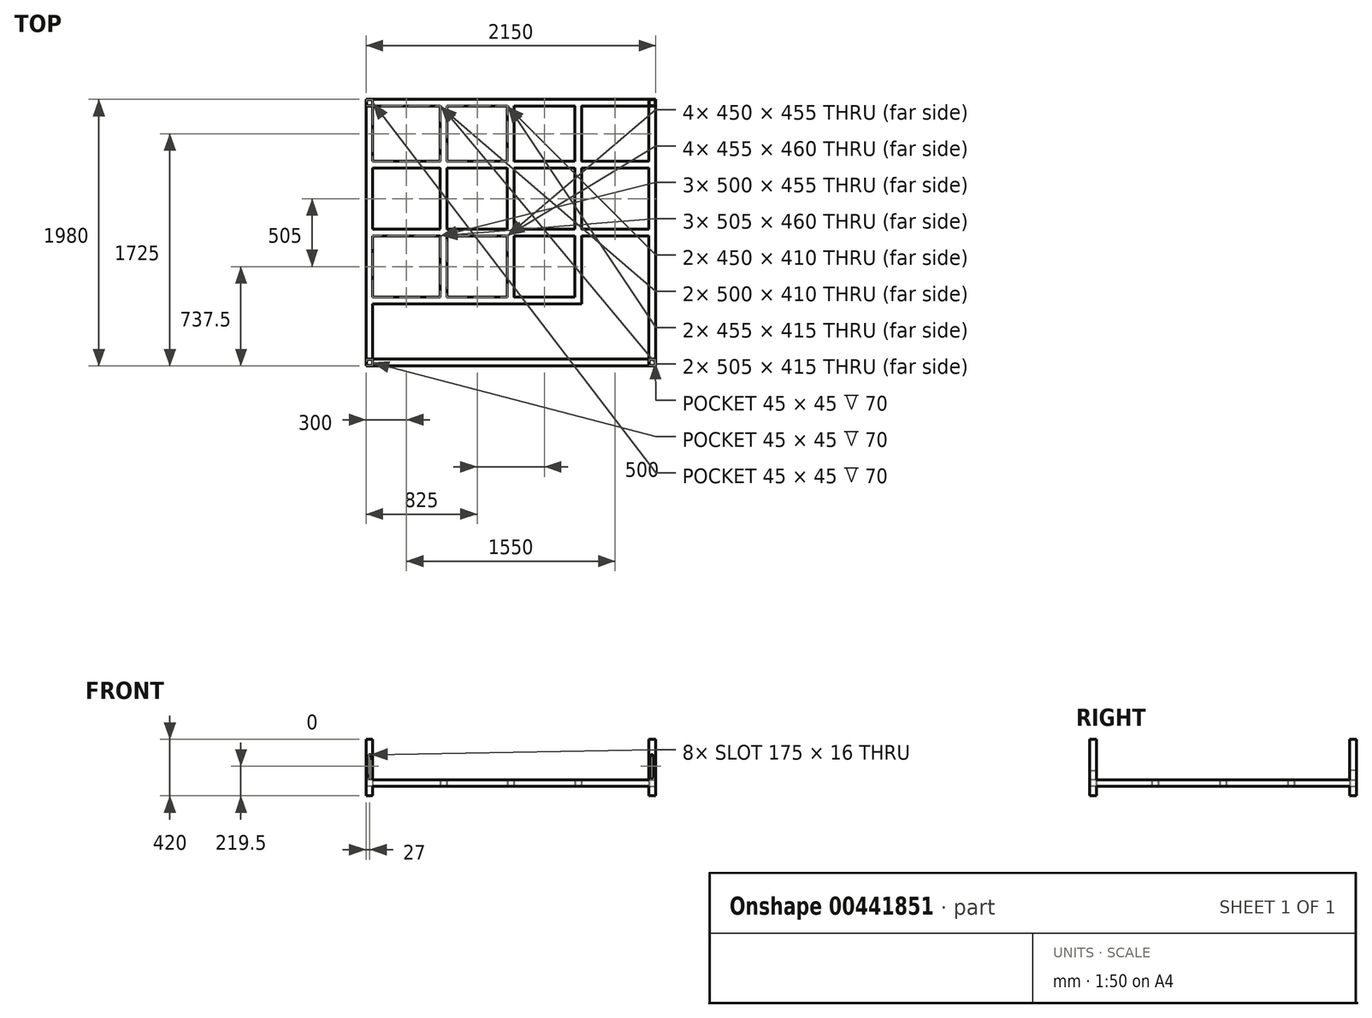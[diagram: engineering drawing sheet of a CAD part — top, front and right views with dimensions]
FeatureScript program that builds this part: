
annotation { "Feature Type Name" : "Feature", "Feature Type Description" : "" }
export const myFeature = defineFeature(function(context is Context, id is Id, definition is map)
    precondition{}
    {
        {
            var Q0;
            Q0=qCreatedBy(makeId("Top.planeOp"),FACE);
            var sketch = newSketch(context, id + "F0", { "sketchPlane" : qUnion([Q0])});
            skLineSegment(sketch, "E0.bottom", {"start": v(1075, 990) * mm, "end": v(-1075, 990) * mm});
            skLineSegment(sketch, "E0.top", {"start": v(1075, -990) * mm, "end": v(-1075, -990) * mm});
            skLineSegment(sketch, "E0.left", {"start": v(1075, 990) * mm, "end": v(1075, -990) * mm});
            skLineSegment(sketch, "E0.right", {"start": v(-1075, 990) * mm, "end": v(-1075, -990) * mm});
            skPoint(sketch, "E0.middle", {"position": v(0, 0) * mm});
            skLineSegment(sketch, "E1.bottom", {"start": v(1025, 940) * mm, "end": v(-1025, 940) * mm});
            skLineSegment(sketch, "E1.top", {"start": v(1025, -940) * mm, "end": v(-1025, -940) * mm});
            skLineSegment(sketch, "E1.left", {"start": v(1025, 940) * mm, "end": v(1025, -940) * mm});
            skLineSegment(sketch, "E1.right", {"start": v(-1025, 940) * mm, "end": v(-1025, -940) * mm});
            skLineSegment(sketch, "E2", {"start": v(-1025, 530) * mm, "end": v(1025, 530) * mm});
            skLineSegment(sketch, "E3", {"start": v(-1025, 480) * mm, "end": v(1025, 480) * mm});
            skLineSegment(sketch, "E4", {"start": v(-1025, 25) * mm, "end": v(1025, 25) * mm});
            skLineSegment(sketch, "E5", {"start": v(-1025, -25) * mm, "end": v(1025, -25) * mm});
            skLineSegment(sketch, "E6", {"start": v(-1025, -480) * mm, "end": v(1025, -480) * mm});
            skLineSegment(sketch, "E7", {"start": v(1025, -480) * mm, "end": v(1025, -530) * mm});
            skLineSegment(sketch, "E8", {"start": v(1025, -530) * mm, "end": v(-1025, -530) * mm});
            skLineSegment(sketch, "E9", {"start": v(-525, 940) * mm, "end": v(-525, -940) * mm});
            skLineSegment(sketch, "E10", {"start": v(-525, -940) * mm, "end": v(-475, -940) * mm});
            skLineSegment(sketch, "E11", {"start": v(-475, -940) * mm, "end": v(-475, 940) * mm});
            skLineSegment(sketch, "E12", {"start": v(-475, 940) * mm, "end": v(-25, 940) * mm});
            skLineSegment(sketch, "E13", {"start": v(-25, 940) * mm, "end": v(-25, -940) * mm});
            skLineSegment(sketch, "E14", {"start": v(-25, -940) * mm, "end": v(25, -940) * mm});
            skLineSegment(sketch, "E15", {"start": v(25, -940) * mm, "end": v(25, 940) * mm});
            skLineSegment(sketch, "E16", {"start": v(25, 940) * mm, "end": v(475, 940) * mm});
            skLineSegment(sketch, "E17", {"start": v(475, 940) * mm, "end": v(475, -940) * mm});
            skLineSegment(sketch, "E18", {"start": v(475, -940) * mm, "end": v(525, -940) * mm});
            skLineSegment(sketch, "E19", {"start": v(525, -940) * mm, "end": v(525, 940) * mm});
            skSolve(sketch);
        }
        {
            var Q0;
            Q0=makeQuery(id+"F0.imprint","IMPRINT",FACE,{"disambiguationData":[TD([[makeQuery(id+"F0.imprint","IMPRINT",EDGE,{"derivedFrom":sQuery(id+"F0.wireOp",EDGE,"E0.bottom")}),1.0]])]});
            var Q1;
            {var subQ0=sQuery(id+"F0.wireOp",EDGE,"E9");var subQ1=sQuery(id+"F0.wireOp",EDGE,"E2");var subQ2=makeQuery(id+"F0.imprint","INTERSECT",VERTEX,{"derivedFrom":[subQ1,subQ0]});Q1=makeQuery(id+"F0.imprint","IMPRINT",FACE,{"disambiguationData":[TD([[makeQuery(id+"F0.imprint","IMPRINT",EDGE,{"disambiguationData":[TD([[subQ2,-1.0]])],"derivedFrom":subQ1}),-1.0]])]});}
            var Q2;
            {var subQ0=sQuery(id+"F0.wireOp",EDGE,"E9");var subQ1=sQuery(id+"F0.wireOp",EDGE,"E4");var subQ2=makeQuery(id+"F0.imprint","INTERSECT",VERTEX,{"derivedFrom":[subQ1,subQ0]});Q2=makeQuery(id+"F0.imprint","IMPRINT",FACE,{"disambiguationData":[TD([[makeQuery(id+"F0.imprint","IMPRINT",EDGE,{"disambiguationData":[TD([[subQ2,-1.0]])],"derivedFrom":subQ1}),-1.0]])]});}
            var Q3;
            {var subQ0=sQuery(id+"F0.wireOp",EDGE,"E11");var subQ1=sQuery(id+"F0.wireOp",EDGE,"E2");var subQ2=makeQuery(id+"F0.imprint","INTERSECT",VERTEX,{"derivedFrom":[subQ1,subQ0]});Q3=makeQuery(id+"F0.imprint","IMPRINT",FACE,{"disambiguationData":[TD([[makeQuery(id+"F0.imprint","IMPRINT",EDGE,{"disambiguationData":[TD([[subQ2,-1.0]])],"derivedFrom":subQ1}),-1.0]])]});}
            var Q4;
            {var subQ0=sQuery(id+"F0.wireOp",EDGE,"E13");var subQ1=sQuery(id+"F0.wireOp",EDGE,"E2");var subQ2=makeQuery(id+"F0.imprint","INTERSECT",VERTEX,{"derivedFrom":[subQ1,subQ0]});Q4=makeQuery(id+"F0.imprint","IMPRINT",FACE,{"disambiguationData":[TD([[makeQuery(id+"F0.imprint","IMPRINT",EDGE,{"disambiguationData":[TD([[subQ2,-1.0]])],"derivedFrom":subQ1}),-1.0]])]});}
            var Q5;
            {var subQ0=sQuery(id+"F0.wireOp",EDGE,"E15");var subQ1=sQuery(id+"F0.wireOp",EDGE,"E2");var subQ2=makeQuery(id+"F0.imprint","INTERSECT",VERTEX,{"derivedFrom":[subQ1,subQ0]});Q5=makeQuery(id+"F0.imprint","IMPRINT",FACE,{"disambiguationData":[TD([[makeQuery(id+"F0.imprint","IMPRINT",EDGE,{"disambiguationData":[TD([[subQ2,-1.0]])],"derivedFrom":subQ1}),-1.0]])]});}
            var Q6;
            {var subQ0=sQuery(id+"F0.wireOp",EDGE,"E17");var subQ1=sQuery(id+"F0.wireOp",EDGE,"E2");var subQ2=makeQuery(id+"F0.imprint","INTERSECT",VERTEX,{"derivedFrom":[subQ1,subQ0]});Q6=makeQuery(id+"F0.imprint","IMPRINT",FACE,{"disambiguationData":[TD([[makeQuery(id+"F0.imprint","IMPRINT",EDGE,{"disambiguationData":[TD([[subQ2,-1.0]])],"derivedFrom":subQ1}),-1.0]])]});}
            var Q7;
            {var subQ0=sQuery(id+"F0.wireOp",EDGE,"E2");var subQ1=sQuery(id+"F0.wireOp",EDGE,"E1.left");var subQ2=makeQuery(id+"F0.imprint","INTERSECT",VERTEX,{"derivedFrom":[subQ1,subQ0]});Q7=makeQuery(id+"F0.imprint","IMPRINT",FACE,{"disambiguationData":[TD([[makeQuery(id+"F0.imprint","IMPRINT",EDGE,{"disambiguationData":[TD([[subQ2,-1.0]])],"derivedFrom":subQ1}),-1.0]])]});}
            var Q8;
            {var subQ0=sQuery(id+"F0.wireOp",EDGE,"E17");var subQ5=sQuery(id+"F0.wireOp",EDGE,"E2");var subQ7=makeQuery(id+"F0.imprint","INTERSECT",VERTEX,{"derivedFrom":[subQ5,subQ0]});Q8=makeQuery(id+"F0.imprint","IMPRINT",FACE,{"disambiguationData":[TD([[makeQuery(id+"F0.imprint","IMPRINT",EDGE,{"disambiguationData":[TD([[subQ7,-1.0]])],"derivedFrom":subQ5}),1.0]])]});}
            var Q9;
            {var subQ0=sQuery(id+"F0.wireOp",EDGE,"E13");var subQ5=sQuery(id+"F0.wireOp",EDGE,"E2");var subQ6=makeQuery(id+"F0.imprint","INTERSECT",VERTEX,{"derivedFrom":[subQ5,subQ0]});Q9=makeQuery(id+"F0.imprint","IMPRINT",FACE,{"disambiguationData":[TD([[makeQuery(id+"F0.imprint","IMPRINT",EDGE,{"disambiguationData":[TD([[subQ6,-1.0]])],"derivedFrom":subQ5}),1.0]])]});}
            var Q10;
            {var subQ0=sQuery(id+"F0.wireOp",EDGE,"E9");var subQ5=sQuery(id+"F0.wireOp",EDGE,"E2");var subQ6=makeQuery(id+"F0.imprint","INTERSECT",VERTEX,{"derivedFrom":[subQ5,subQ0]});Q10=makeQuery(id+"F0.imprint","IMPRINT",FACE,{"disambiguationData":[TD([[makeQuery(id+"F0.imprint","IMPRINT",EDGE,{"disambiguationData":[TD([[subQ6,-1.0]])],"derivedFrom":subQ5}),1.0]])]});}
            var Q11;
            {var subQ0=sQuery(id+"F0.wireOp",EDGE,"E2");var subQ1=sQuery(id+"F0.wireOp",EDGE,"E1.right");var subQ2=makeQuery(id+"F0.imprint","INTERSECT",VERTEX,{"derivedFrom":[subQ1,subQ0]});Q11=makeQuery(id+"F0.imprint","IMPRINT",FACE,{"disambiguationData":[TD([[makeQuery(id+"F0.imprint","IMPRINT",EDGE,{"disambiguationData":[TD([[subQ2,-1.0]])],"derivedFrom":subQ1}),1.0]])]});}
            var Q12;
            {var subQ0=sQuery(id+"F0.wireOp",EDGE,"E4");var subQ1=sQuery(id+"F0.wireOp",EDGE,"E1.right");var subQ2=makeQuery(id+"F0.imprint","INTERSECT",VERTEX,{"derivedFrom":[subQ1,subQ0]});Q12=makeQuery(id+"F0.imprint","IMPRINT",FACE,{"disambiguationData":[TD([[makeQuery(id+"F0.imprint","IMPRINT",EDGE,{"disambiguationData":[TD([[subQ2,-1.0]])],"derivedFrom":subQ1}),1.0]])]});}
            var Q13;
            {var subQ0=sQuery(id+"F0.wireOp",EDGE,"E9");var subQ1=sQuery(id+"F0.wireOp",EDGE,"E3");var subQ2=makeQuery(id+"F0.imprint","INTERSECT",VERTEX,{"derivedFrom":[subQ1,subQ0]});Q13=makeQuery(id+"F0.imprint","IMPRINT",FACE,{"disambiguationData":[TD([[makeQuery(id+"F0.imprint","IMPRINT",EDGE,{"disambiguationData":[TD([[subQ2,-1.0]])],"derivedFrom":subQ1}),-1.0]])]});}
            var Q14;
            {var subQ0=sQuery(id+"F0.wireOp",EDGE,"E9");var subQ1=sQuery(id+"F0.wireOp",EDGE,"E5");var subQ2=makeQuery(id+"F0.imprint","INTERSECT",VERTEX,{"derivedFrom":[subQ1,subQ0]});Q14=makeQuery(id+"F0.imprint","IMPRINT",FACE,{"disambiguationData":[TD([[makeQuery(id+"F0.imprint","IMPRINT",EDGE,{"disambiguationData":[TD([[subQ2,-1.0]])],"derivedFrom":subQ1}),-1.0]])]});}
            var Q15;
            {var subQ0=sQuery(id+"F0.wireOp",EDGE,"E11");var subQ1=sQuery(id+"F0.wireOp",EDGE,"E4");var subQ2=makeQuery(id+"F0.imprint","INTERSECT",VERTEX,{"derivedFrom":[subQ1,subQ0]});Q15=makeQuery(id+"F0.imprint","IMPRINT",FACE,{"disambiguationData":[TD([[makeQuery(id+"F0.imprint","IMPRINT",EDGE,{"disambiguationData":[TD([[subQ2,-1.0]])],"derivedFrom":subQ1}),-1.0]])]});}
            var Q16;
            {var subQ0=sQuery(id+"F0.wireOp",EDGE,"E13");var subQ1=sQuery(id+"F0.wireOp",EDGE,"E3");var subQ2=makeQuery(id+"F0.imprint","INTERSECT",VERTEX,{"derivedFrom":[subQ1,subQ0]});Q16=makeQuery(id+"F0.imprint","IMPRINT",FACE,{"disambiguationData":[TD([[makeQuery(id+"F0.imprint","IMPRINT",EDGE,{"disambiguationData":[TD([[subQ2,-1.0]])],"derivedFrom":subQ1}),-1.0]])]});}
            var Q17;
            {var subQ0=sQuery(id+"F0.wireOp",EDGE,"E15");var subQ1=sQuery(id+"F0.wireOp",EDGE,"E4");var subQ2=makeQuery(id+"F0.imprint","INTERSECT",VERTEX,{"derivedFrom":[subQ1,subQ0]});Q17=makeQuery(id+"F0.imprint","IMPRINT",FACE,{"disambiguationData":[TD([[makeQuery(id+"F0.imprint","IMPRINT",EDGE,{"disambiguationData":[TD([[subQ2,-1.0]])],"derivedFrom":subQ1}),-1.0]])]});}
            var Q18;
            {var subQ0=sQuery(id+"F0.wireOp",EDGE,"E17");var subQ1=sQuery(id+"F0.wireOp",EDGE,"E4");var subQ2=makeQuery(id+"F0.imprint","INTERSECT",VERTEX,{"derivedFrom":[subQ1,subQ0]});Q18=makeQuery(id+"F0.imprint","IMPRINT",FACE,{"disambiguationData":[TD([[makeQuery(id+"F0.imprint","IMPRINT",EDGE,{"disambiguationData":[TD([[subQ2,-1.0]])],"derivedFrom":subQ1}),-1.0]])]});}
            var Q19;
            {var subQ0=sQuery(id+"F0.wireOp",EDGE,"E17");var subQ1=sQuery(id+"F0.wireOp",EDGE,"E3");var subQ2=makeQuery(id+"F0.imprint","INTERSECT",VERTEX,{"derivedFrom":[subQ1,subQ0]});Q19=makeQuery(id+"F0.imprint","IMPRINT",FACE,{"disambiguationData":[TD([[makeQuery(id+"F0.imprint","IMPRINT",EDGE,{"disambiguationData":[TD([[subQ2,-1.0]])],"derivedFrom":subQ1}),-1.0]])]});}
            var Q20;
            {var subQ0=sQuery(id+"F0.wireOp",EDGE,"E4");var subQ1=sQuery(id+"F0.wireOp",EDGE,"E1.left");var subQ2=makeQuery(id+"F0.imprint","INTERSECT",VERTEX,{"derivedFrom":[subQ1,subQ0]});Q20=makeQuery(id+"F0.imprint","IMPRINT",FACE,{"disambiguationData":[TD([[makeQuery(id+"F0.imprint","IMPRINT",EDGE,{"disambiguationData":[TD([[subQ2,-1.0]])],"derivedFrom":subQ1}),-1.0]])]});}
            var Q21;
            {var subQ0=sQuery(id+"F0.wireOp",EDGE,"E17");var subQ1=sQuery(id+"F0.wireOp",EDGE,"E5");var subQ2=makeQuery(id+"F0.imprint","INTERSECT",VERTEX,{"derivedFrom":[subQ1,subQ0]});Q21=makeQuery(id+"F0.imprint","IMPRINT",FACE,{"disambiguationData":[TD([[makeQuery(id+"F0.imprint","IMPRINT",EDGE,{"disambiguationData":[TD([[subQ2,-1.0]])],"derivedFrom":subQ1}),-1.0]])]});}
            var Q22;
            {var subQ0=sQuery(id+"F0.wireOp",EDGE,"E7");Q22=makeQuery(id+"F0.imprint","IMPRINT",FACE,{"disambiguationData":[TD([[makeQuery(id+"F0.imprint","IMPRINT",EDGE,{"derivedFrom":subQ0}),-1.0]])]});}
            var Q23;
            {var subQ0=sQuery(id+"F0.wireOp",EDGE,"E17");var subQ1=sQuery(id+"F0.wireOp",EDGE,"E6");var subQ2=makeQuery(id+"F0.imprint","INTERSECT",VERTEX,{"derivedFrom":[subQ1,subQ0]});Q23=makeQuery(id+"F0.imprint","IMPRINT",FACE,{"disambiguationData":[TD([[makeQuery(id+"F0.imprint","IMPRINT",EDGE,{"disambiguationData":[TD([[subQ2,-1.0]])],"derivedFrom":subQ1}),-1.0]])]});}
            var Q24;
            {var subQ5=sQuery(id+"F0.wireOp",EDGE,"E18");Q24=makeQuery(id+"F0.imprint","IMPRINT",FACE,{"disambiguationData":[TD([[makeQuery(id+"F0.imprint","IMPRINT",EDGE,{"derivedFrom":subQ5}),1.0]])]});}
            var Q25;
            {var subQ0=sQuery(id+"F0.wireOp",EDGE,"E15");var subQ1=sQuery(id+"F0.wireOp",EDGE,"E6");var subQ2=makeQuery(id+"F0.imprint","INTERSECT",VERTEX,{"derivedFrom":[subQ1,subQ0]});Q25=makeQuery(id+"F0.imprint","IMPRINT",FACE,{"disambiguationData":[TD([[makeQuery(id+"F0.imprint","IMPRINT",EDGE,{"disambiguationData":[TD([[subQ2,-1.0]])],"derivedFrom":subQ1}),-1.0]])]});}
            var Q26;
            {var subQ0=sQuery(id+"F0.wireOp",EDGE,"E13");var subQ1=sQuery(id+"F0.wireOp",EDGE,"E6");var subQ2=makeQuery(id+"F0.imprint","INTERSECT",VERTEX,{"derivedFrom":[subQ1,subQ0]});Q26=makeQuery(id+"F0.imprint","IMPRINT",FACE,{"disambiguationData":[TD([[makeQuery(id+"F0.imprint","IMPRINT",EDGE,{"disambiguationData":[TD([[subQ2,-1.0]])],"derivedFrom":subQ1}),-1.0]])]});}
            var Q27;
            {var subQ0=sQuery(id+"F0.wireOp",EDGE,"E13");var subQ1=sQuery(id+"F0.wireOp",EDGE,"E5");var subQ2=makeQuery(id+"F0.imprint","INTERSECT",VERTEX,{"derivedFrom":[subQ1,subQ0]});Q27=makeQuery(id+"F0.imprint","IMPRINT",FACE,{"disambiguationData":[TD([[makeQuery(id+"F0.imprint","IMPRINT",EDGE,{"disambiguationData":[TD([[subQ2,-1.0]])],"derivedFrom":subQ1}),-1.0]])]});}
            var Q28;
            {var subQ5=sQuery(id+"F0.wireOp",EDGE,"E14");Q28=makeQuery(id+"F0.imprint","IMPRINT",FACE,{"disambiguationData":[TD([[makeQuery(id+"F0.imprint","IMPRINT",EDGE,{"derivedFrom":subQ5}),1.0]])]});}
            var Q29;
            {var subQ0=sQuery(id+"F0.wireOp",EDGE,"E11");var subQ1=sQuery(id+"F0.wireOp",EDGE,"E6");var subQ2=makeQuery(id+"F0.imprint","INTERSECT",VERTEX,{"derivedFrom":[subQ1,subQ0]});Q29=makeQuery(id+"F0.imprint","IMPRINT",FACE,{"disambiguationData":[TD([[makeQuery(id+"F0.imprint","IMPRINT",EDGE,{"disambiguationData":[TD([[subQ2,-1.0]])],"derivedFrom":subQ1}),-1.0]])]});}
            var Q30;
            {var subQ0=sQuery(id+"F0.wireOp",EDGE,"E9");var subQ1=sQuery(id+"F0.wireOp",EDGE,"E6");var subQ2=makeQuery(id+"F0.imprint","INTERSECT",VERTEX,{"derivedFrom":[subQ1,subQ0]});Q30=makeQuery(id+"F0.imprint","IMPRINT",FACE,{"disambiguationData":[TD([[makeQuery(id+"F0.imprint","IMPRINT",EDGE,{"disambiguationData":[TD([[subQ2,-1.0]])],"derivedFrom":subQ1}),-1.0]])]});}
            var Q31;
            {var subQ0=sQuery(id+"F0.wireOp",EDGE,"E6");var subQ1=sQuery(id+"F0.wireOp",EDGE,"E1.right");var subQ2=makeQuery(id+"F0.imprint","INTERSECT",VERTEX,{"derivedFrom":[subQ1,subQ0]});Q31=makeQuery(id+"F0.imprint","IMPRINT",FACE,{"disambiguationData":[TD([[makeQuery(id+"F0.imprint","IMPRINT",EDGE,{"disambiguationData":[TD([[subQ2,-1.0]])],"derivedFrom":subQ1}),1.0]])]});}
            var Q32;
            {var subQ5=sQuery(id+"F0.wireOp",EDGE,"E10");Q32=makeQuery(id+"F0.imprint","IMPRINT",FACE,{"disambiguationData":[TD([[makeQuery(id+"F0.imprint","IMPRINT",EDGE,{"derivedFrom":subQ5}),1.0]])]});}
            var Q33;
            {var subQ0=sQuery(id+"F0.wireOp",EDGE,"E13");var subQ1=sQuery(id+"F0.wireOp",EDGE,"E4");var subQ2=makeQuery(id+"F0.imprint","INTERSECT",VERTEX,{"derivedFrom":[subQ1,subQ0]});Q33=makeQuery(id+"F0.imprint","IMPRINT",FACE,{"disambiguationData":[TD([[makeQuery(id+"F0.imprint","IMPRINT",EDGE,{"disambiguationData":[TD([[subQ2,-1.0]])],"derivedFrom":subQ1}),-1.0]])]});}
            extrude(context, id + "F1", {"entities" : qUnion([Q0, Q1, Q2, Q3, Q4, Q5, Q6, Q7, Q8, Q9, Q10, Q11, Q12, Q13, Q14, Q15, Q16, Q17, Q18, Q19, Q20, Q21, Q22, Q23, Q24, Q25, Q26, Q27, Q28, Q29, Q30, Q31, Q32, Q33]), "depth" : 50 * mm});
        }
        {
            var Q0;
            Q0=makeQuery(id+"F1.opExtrude","CAP_FACE",FACE,{"disambiguationData":[OSD([sQuery(id+"F0.wireOp",EDGE,"E0.bottom"),sQuery(id+"F0.wireOp",EDGE,"E0.top"),sQuery(id+"F0.wireOp",EDGE,"E0.left"),sQuery(id+"F0.wireOp",EDGE,"E0.right"),sQuery(id+"F0.wireOp",EDGE,"E1.bottom"),sQuery(id+"F0.wireOp",EDGE,"E1.top"),sQuery(id+"F0.wireOp",EDGE,"E1.left"),sQuery(id+"F0.wireOp",EDGE,"E1.right"),sQuery(id+"F0.wireOp",EDGE,"E2"),sQuery(id+"F0.wireOp",EDGE,"E3"),sQuery(id+"F0.wireOp",EDGE,"E4"),sQuery(id+"F0.wireOp",EDGE,"E5"),sQuery(id+"F0.wireOp",EDGE,"E6"),sQuery(id+"F0.wireOp",EDGE,"E8"),sQuery(id+"F0.wireOp",EDGE,"E9"),sQuery(id+"F0.wireOp",EDGE,"E11"),sQuery(id+"F0.wireOp",EDGE,"E12"),sQuery(id+"F0.wireOp",EDGE,"E13"),sQuery(id+"F0.wireOp",EDGE,"E15"),sQuery(id+"F0.wireOp",EDGE,"E16"),sQuery(id+"F0.wireOp",EDGE,"E17"),sQuery(id+"F0.wireOp",EDGE,"E19")])],"isStart":false});
            var sketch = newSketch(context, id + "F2", { "sketchPlane" : qUnion([Q0])});
            skLineSegment(sketch, "E20.bottom", {"start": v(1075, 990) * mm, "end": v(1025, 990) * mm});
            skLineSegment(sketch, "E20.top", {"start": v(1075, 940) * mm, "end": v(1025, 940) * mm});
            skLineSegment(sketch, "E20.left", {"start": v(1075, 990) * mm, "end": v(1075, 940) * mm});
            skLineSegment(sketch, "E20.right", {"start": v(1025, 990) * mm, "end": v(1025, 940) * mm});
            skLineSegment(sketch, "E21.bottom", {"start": v(1075, -990) * mm, "end": v(1025, -990) * mm});
            skLineSegment(sketch, "E21.top", {"start": v(1075, -940) * mm, "end": v(1025, -940) * mm});
            skLineSegment(sketch, "E21.left", {"start": v(1075, -990) * mm, "end": v(1075, -940) * mm});
            skLineSegment(sketch, "E21.right", {"start": v(1025, -990) * mm, "end": v(1025, -940) * mm});
            skLineSegment(sketch, "E22.bottom", {"start": v(-1075, -990) * mm, "end": v(-1025, -990) * mm});
            skLineSegment(sketch, "E22.top", {"start": v(-1075, -940) * mm, "end": v(-1025, -940) * mm});
            skLineSegment(sketch, "E22.left", {"start": v(-1075, -990) * mm, "end": v(-1075, -940) * mm});
            skLineSegment(sketch, "E22.right", {"start": v(-1025, -990) * mm, "end": v(-1025, -940) * mm});
            skLineSegment(sketch, "E23.bottom", {"start": v(-1075, 990) * mm, "end": v(-1025, 990) * mm});
            skLineSegment(sketch, "E23.top", {"start": v(-1075, 940) * mm, "end": v(-1025, 940) * mm});
            skLineSegment(sketch, "E23.left", {"start": v(-1075, 990) * mm, "end": v(-1075, 940) * mm});
            skLineSegment(sketch, "E23.right", {"start": v(-1025, 990) * mm, "end": v(-1025, 940) * mm});
            skSolve(sketch);
        }
        {
            var Q0;
            Q0 = qSketchRegion(id + "F2", true);
            extrude(context, id + "F3", {"entities" : qUnion([Q0]), "operationType" : NewBodyOperationType.ADD, "depth" : 300 * mm, "hasSecondDirection" : true, "secondDirectionOppositeDirection" : true, "secondDirectionDepth" : 120 * mm});
        }
        {
            var Q0;
            Q0=makeQuery(id+"F3.opExtrude","CAP_FACE",FACE,{"disambiguationData":[OSD([sQuery(id+"F2.wireOp",EDGE,"E22.bottom"),sQuery(id+"F2.wireOp",EDGE,"E22.top"),sQuery(id+"F2.wireOp",EDGE,"E22.left"),sQuery(id+"F2.wireOp",EDGE,"E22.right")])],"isStart":false});
            var Q1;
            Q1=makeQuery(id+"F3.opExtrude","CAP_FACE",FACE,{"disambiguationData":[OSD([sQuery(id+"F2.wireOp",EDGE,"E21.bottom"),sQuery(id+"F2.wireOp",EDGE,"E21.top"),sQuery(id+"F2.wireOp",EDGE,"E21.left"),sQuery(id+"F2.wireOp",EDGE,"E21.right")])],"isStart":false});
            var Q2;
            Q2=makeQuery(id+"F3.opExtrude","CAP_FACE",FACE,{"disambiguationData":[OSD([sQuery(id+"F2.wireOp",EDGE,"E20.bottom"),sQuery(id+"F2.wireOp",EDGE,"E20.top"),sQuery(id+"F2.wireOp",EDGE,"E20.left"),sQuery(id+"F2.wireOp",EDGE,"E20.right")])],"isStart":false});
            var Q3;
            Q3=makeQuery(id+"F3.opExtrude","CAP_FACE",FACE,{"disambiguationData":[OSD([sQuery(id+"F2.wireOp",EDGE,"E23.bottom"),sQuery(id+"F2.wireOp",EDGE,"E23.top"),sQuery(id+"F2.wireOp",EDGE,"E23.left"),sQuery(id+"F2.wireOp",EDGE,"E23.right")])],"isStart":false});
            shell(context, id + "F4", {"entities" : qUnion([Q0, Q1, Q2, Q3]), "thickness" : 2.5 * mm});
        }
        {
            var Q0;
            {var subQ6=sQuery(id+"F2.wireOp",EDGE,"E22.bottom");var subQ7=sQuery(id+"F2.wireOp",EDGE,"E22.right");var subQ8=sQuery(id+"F2.wireOp",EDGE,"E22.top");Q0=makeQuery(id+"F3.boolean.opBoolean","SPLIT",FACE,{"disambiguationData":[TD([makeQuery(id+"F3.opExtrude","CAP_FACE",FACE,{"disambiguationData":[OSD([subQ6,subQ8,sQuery(id+"F2.wireOp",EDGE,"E22.left"),subQ7])],"isStart":false})])],"derivedFrom":makeQuery(id+"F3.opExtrude","SWEPT_FACE",FACE,{"disambiguationData":[OSD([subQ7])]})});}
            var sketch = newSketch(context, id + "F5", { "sketchPlane" : qUnion([Q0])});
            skLineSegment(sketch, "E24.bottom", {"start": v(-987.5, 350) * mm, "end": v(-942.5, 350) * mm});
            skLineSegment(sketch, "E24.top", {"start": v(-987.5, 120) * mm, "end": v(-942.5, 120) * mm});
            skLineSegment(sketch, "E24.left", {"start": v(-987.5, 350) * mm, "end": v(-987.5, 120) * mm});
            skLineSegment(sketch, "E24.right", {"start": v(-942.5, 350) * mm, "end": v(-942.5, 120) * mm});
            skSolve(sketch);
        }
        {
            var Q0;
            Q0=makeQuery(id+"F5.imprint","IMPRINT",FACE,{"disambiguationData":[TD([[makeQuery(id+"F5.imprint","IMPRINT",EDGE,{"derivedFrom":sQuery(id+"F5.wireOp",EDGE,"E24.bottom")}),-1.0]])]});
            extrude(context, id + "F6", {"entities" : qUnion([Q0]), "operationType" : NewBodyOperationType.REMOVE, "oppositeDirection" : true, "depth" : 25 * mm});
        }
        {
            var Q0;
            {var subQ6=sQuery(id+"F2.wireOp",EDGE,"E23.top");var subQ7=sQuery(id+"F2.wireOp",EDGE,"E23.bottom");var subQ8=sQuery(id+"F2.wireOp",EDGE,"E23.right");Q0=makeQuery(id+"F3.boolean.opBoolean","SPLIT",FACE,{"disambiguationData":[TD([makeQuery(id+"F3.opExtrude","CAP_FACE",FACE,{"disambiguationData":[OSD([subQ7,subQ6,sQuery(id+"F2.wireOp",EDGE,"E23.left"),subQ8])],"isStart":false})])],"derivedFrom":makeQuery(id+"F3.opExtrude","SWEPT_FACE",FACE,{"disambiguationData":[OSD([subQ8])]})});}
            var sketch = newSketch(context, id + "F7", { "sketchPlane" : qUnion([Q0])});
            skLineSegment(sketch, "E25.bottom", {"start": v(942.5, 350) * mm, "end": v(987.5, 350) * mm});
            skLineSegment(sketch, "E25.top", {"start": v(942.5, 120) * mm, "end": v(987.5, 120) * mm});
            skLineSegment(sketch, "E25.left", {"start": v(942.5, 350) * mm, "end": v(942.5, 120) * mm});
            skLineSegment(sketch, "E25.right", {"start": v(987.5, 350) * mm, "end": v(987.5, 120) * mm});
            skSolve(sketch);
        }
        {
            var Q0;
            Q0=makeQuery(id+"F7.imprint","IMPRINT",FACE,{"disambiguationData":[TD([[makeQuery(id+"F7.imprint","IMPRINT",EDGE,{"derivedFrom":sQuery(id+"F7.wireOp",EDGE,"E25.bottom")}),1.0]])]});
            extrude(context, id + "F8", {"entities" : qUnion([Q0]), "operationType" : NewBodyOperationType.REMOVE, "oppositeDirection" : true, "depth" : 25 * mm});
        }
        {
            var Q0;
            {var subQ6=sQuery(id+"F2.wireOp",EDGE,"E21.bottom");var subQ7=sQuery(id+"F2.wireOp",EDGE,"E21.right");var subQ8=sQuery(id+"F2.wireOp",EDGE,"E21.top");Q0=makeQuery(id+"F3.boolean.opBoolean","SPLIT",FACE,{"disambiguationData":[TD([makeQuery(id+"F3.opExtrude","CAP_FACE",FACE,{"disambiguationData":[OSD([subQ6,subQ8,sQuery(id+"F2.wireOp",EDGE,"E21.left"),subQ7])],"isStart":false})])],"derivedFrom":makeQuery(id+"F3.opExtrude","SWEPT_FACE",FACE,{"disambiguationData":[OSD([subQ7])]})});}
            var sketch = newSketch(context, id + "F9", { "sketchPlane" : qUnion([Q0])});
            skLineSegment(sketch, "E26.bottom", {"start": v(942.5, 350) * mm, "end": v(987.5, 350) * mm});
            skLineSegment(sketch, "E26.top", {"start": v(942.5, 120) * mm, "end": v(987.5, 120) * mm});
            skLineSegment(sketch, "E26.left", {"start": v(942.5, 350) * mm, "end": v(942.5, 120) * mm});
            skLineSegment(sketch, "E26.right", {"start": v(987.5, 350) * mm, "end": v(987.5, 120) * mm});
            skSolve(sketch);
        }
        {
            var Q0;
            Q0=makeQuery(id+"F9.imprint","IMPRINT",FACE,{"disambiguationData":[TD([[makeQuery(id+"F9.imprint","IMPRINT",EDGE,{"derivedFrom":sQuery(id+"F9.wireOp",EDGE,"E26.bottom")}),1.0]])]});
            extrude(context, id + "F10", {"entities" : qUnion([Q0]), "operationType" : NewBodyOperationType.REMOVE, "oppositeDirection" : true, "depth" : 25 * mm});
        }
        {
            var Q0;
            {var subQ5=sQuery(id+"F2.wireOp",EDGE,"E20.bottom");var subQ7=sQuery(id+"F2.wireOp",EDGE,"E20.right");var subQ8=sQuery(id+"F2.wireOp",EDGE,"E20.top");Q0=makeQuery(id+"F3.boolean.opBoolean","SPLIT",FACE,{"disambiguationData":[TD([makeQuery(id+"F3.opExtrude","CAP_FACE",FACE,{"disambiguationData":[OSD([subQ5,subQ8,sQuery(id+"F2.wireOp",EDGE,"E20.left"),subQ7])],"isStart":false})])],"derivedFrom":makeQuery(id+"F3.opExtrude","SWEPT_FACE",FACE,{"disambiguationData":[OSD([subQ7])]})});}
            var sketch = newSketch(context, id + "F11", { "sketchPlane" : qUnion([Q0])});
            skLineSegment(sketch, "E27.bottom", {"start": v(-987.5, 350) * mm, "end": v(-942.5, 350) * mm});
            skLineSegment(sketch, "E27.top", {"start": v(-987.5, 120) * mm, "end": v(-942.5, 120) * mm});
            skLineSegment(sketch, "E27.left", {"start": v(-987.5, 350) * mm, "end": v(-987.5, 120) * mm});
            skLineSegment(sketch, "E27.right", {"start": v(-942.5, 350) * mm, "end": v(-942.5, 120) * mm});
            skSolve(sketch);
        }
        {
            var Q0;
            Q0=makeQuery(id+"F11.imprint","IMPRINT",FACE,{"disambiguationData":[TD([[makeQuery(id+"F11.imprint","IMPRINT",EDGE,{"derivedFrom":sQuery(id+"F11.wireOp",EDGE,"E27.bottom")}),-1.0]])]});
            extrude(context, id + "F12", {"entities" : qUnion([Q0]), "operationType" : NewBodyOperationType.REMOVE, "oppositeDirection" : true, "depth" : 25 * mm});
        }
        {
            var Q0;
            Q0=makeQuery(id+"F3.boolean.opBoolean","MERGE",FACE,{"derivedFrom":[makeQuery(id+"F1.opExtrude","SWEPT_FACE",FACE,{"disambiguationData":[OSD([sQuery(id+"F0.wireOp",EDGE,"E0.bottom")])]}),makeQuery(id+"F3.opExtrude","SWEPT_FACE",FACE,{"disambiguationData":[OSD([sQuery(id+"F2.wireOp",EDGE,"E20.bottom")])]}),makeQuery(id+"F3.opExtrude","SWEPT_FACE",FACE,{"disambiguationData":[OSD([sQuery(id+"F2.wireOp",EDGE,"E23.bottom")])]})]});
            var sketch = newSketch(context, id + "F13", { "sketchPlane" : qUnion([Q0])});
            skLineSegment(sketch, "E28.bottom", {"start": v(-1056, 229) * mm, "end": v(-1040, 229) * mm});
            skLineSegment(sketch, "E28.top", {"start": v(-1056, 70) * mm, "end": v(-1040, 70) * mm});
            skLineSegment(sketch, "E28.left", {"start": v(-1056, 229) * mm, "end": v(-1056, 70) * mm});
            skLineSegment(sketch, "E28.right", {"start": v(-1040, 229) * mm, "end": v(-1040, 70) * mm});
            skArc(sketch, "E29", {"start": v(-1040, 229) * mm, "mid": v(-1048, 237) * mm, "end": v(-1056, 229) * mm});
            skArc(sketch, "E30", {"start": v(-1056, 70) * mm, "mid": v(-1048, 62) * mm, "end": v(-1040, 70) * mm});
            skLineSegment(sketch, "E31.MirrorCS", {"start": v(1040, 229) * mm, "end": v(1040, 70) * mm});
            skArc(sketch, "E32.MirrorCS", {"start": v(1056, 70) * mm, "mid": v(1048, 62) * mm, "end": v(1040, 70) * mm});
            skLineSegment(sketch, "E33.MirrorCS", {"start": v(1056, 229) * mm, "end": v(1056, 70) * mm});
            skArc(sketch, "E34.MirrorCS", {"start": v(1040, 229) * mm, "mid": v(1048, 237) * mm, "end": v(1056, 229) * mm});
            skSolve(sketch);
        }
        {
            var Q0;
            Q0=makeQuery(id+"F13.imprint","IMPRINT",FACE,{"disambiguationData":[TD([[makeQuery(id+"F13.imprint","IMPRINT",EDGE,{"derivedFrom":sQuery(id+"F13.wireOp",EDGE,"E28.bottom")}),1.0]])]});
            var Q1;
            Q1=makeQuery(id+"F13.imprint","IMPRINT",FACE,{"disambiguationData":[TD([[makeQuery(id+"F13.imprint","IMPRINT",EDGE,{"derivedFrom":sQuery(id+"F13.wireOp",EDGE,"E28.bottom")}),-1.0]])]});
            var Q2;
            Q2=makeQuery(id+"F13.imprint","IMPRINT",FACE,{"disambiguationData":[TD([[makeQuery(id+"F13.imprint","IMPRINT",EDGE,{"derivedFrom":sQuery(id+"F13.wireOp",EDGE,"E28.top")}),-1.0]])]});
            var Q3;
            Q3=makeQuery(id+"F13.imprint","IMPRINT",FACE,{"disambiguationData":[TD([[makeQuery(id+"F13.imprint","IMPRINT",EDGE,{"derivedFrom":sQuery(id+"F13.wireOp",EDGE,"E31.MirrorCS")}),1.0]])]});
            var Q4;
            Q4=makeQuery(id+"F3.boolean.opBoolean","MERGE",FACE,{"derivedFrom":[makeQuery(id+"F1.opExtrude","SWEPT_FACE",FACE,{"disambiguationData":[OSD([sQuery(id+"F0.wireOp",EDGE,"E0.top")])]}),makeQuery(id+"F3.opExtrude","SWEPT_FACE",FACE,{"disambiguationData":[OSD([sQuery(id+"F2.wireOp",EDGE,"E21.bottom")])]}),makeQuery(id+"F3.opExtrude","SWEPT_FACE",FACE,{"disambiguationData":[OSD([sQuery(id+"F2.wireOp",EDGE,"E22.bottom")])]})]});
            extrude(context, id + "F14", {"entities" : qUnion([Q0, Q1, Q2, Q3]), "operationType" : NewBodyOperationType.REMOVE, "endBound" : BoundingType.UP_TO_SURFACE, "oppositeDirection" : true, "endBoundEntityFace" : qUnion([Q4]), "depth" : 25 * mm});
        }
    });
